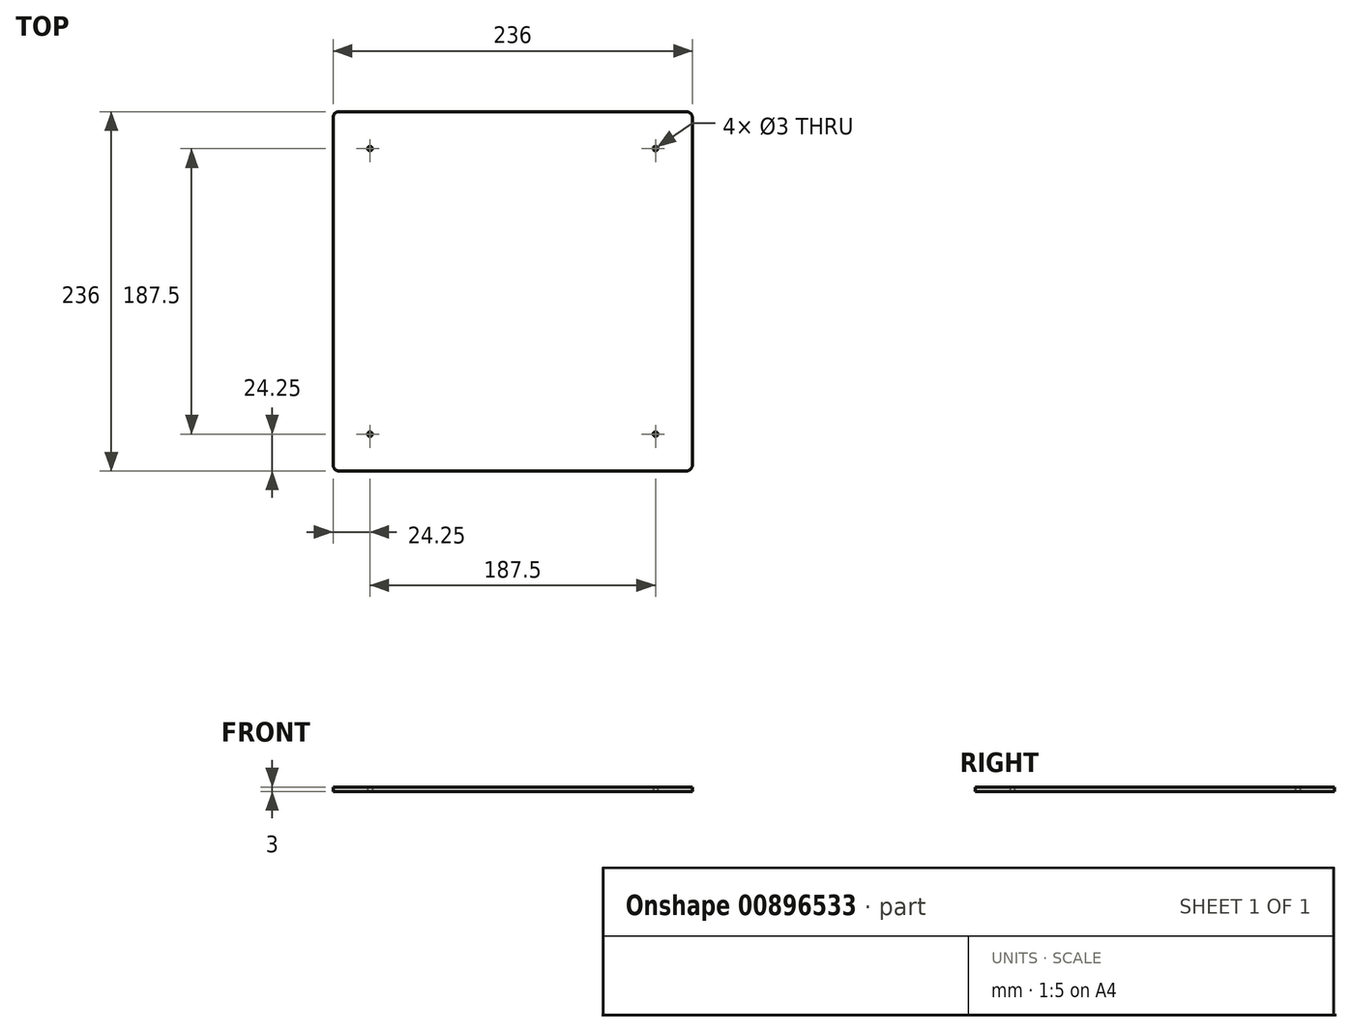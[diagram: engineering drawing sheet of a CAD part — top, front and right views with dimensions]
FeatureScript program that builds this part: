
annotation { "Feature Type Name" : "Feature", "Feature Type Description" : "" }
export const myFeature = defineFeature(function(context is Context, id is Id, definition is map)
    precondition{}
    {
        {
            assignVariable(context, id + "F0", {"variableType" : VariableType.LENGTH, "name" : "thickness", "lengthValue" : 3 * mm});
        }
        {
            var Q0;
            Q0=qCreatedBy(makeId("Top.planeOp"),FACE);
            var sketch = newSketch(context, id + "F1", { "sketchPlane" : qUnion([Q0])});
            skLineSegment(sketch, "E0.bottom", {"start": v(0, 0) * mm, "end": v(236, 0) * mm});
            skLineSegment(sketch, "E0.top", {"start": v(0, 236) * mm, "end": v(236, 236) * mm});
            skLineSegment(sketch, "E0.left", {"start": v(0, 0) * mm, "end": v(0, 236) * mm});
            skLineSegment(sketch, "E0.right", {"start": v(236, 0) * mm, "end": v(236, 236) * mm});
            skLineSegment(sketch, "E1.bottom", {"start": v(24.25, 24.25) * mm, "end": v(211.75, 24.25) * mm, "construction": true});
            skLineSegment(sketch, "E1.top", {"start": v(24.25, 211.75) * mm, "end": v(211.75, 211.75) * mm, "construction": true});
            skLineSegment(sketch, "E1.left", {"start": v(24.25, 24.25) * mm, "end": v(24.25, 211.75) * mm, "construction": true});
            skLineSegment(sketch, "E1.right", {"start": v(211.75, 24.25) * mm, "end": v(211.75, 211.75) * mm, "construction": true});
            skLineSegment(sketch, "E2", {"start": v(118, 236) * mm, "end": v(118, 211.75) * mm, "construction": true});
            skLineSegment(sketch, "E3", {"start": v(211.75, 118) * mm, "end": v(236, 118) * mm, "construction": true});
            skCircle(sketch, "E4", {"center": v(24.25, 211.75) * mm, "radius": 1.5 * mm});
            skCircle(sketch, "E5", {"center": v(211.75, 211.75) * mm, "radius": 1.5 * mm});
            skCircle(sketch, "E6", {"center": v(211.75, 24.25) * mm, "radius": 1.5 * mm});
            skCircle(sketch, "E7", {"center": v(24.25, 24.25) * mm, "radius": 1.5 * mm});
            skSolve(sketch);
        }
        {
            var Q0;
            Q0=qSketchRegion(id+"F1",true);
            extrude(context, id + "F2", {"entities" : qUnion([Q0]), "depth" : getVariable(context, 'thickness'), "offsetDistance" : 25 * mm});
        }
        {
            var Q0;
            Q0=makeQuery(id+"F2.opExtrude","SWEPT_EDGE",EDGE,{"disambiguationData":[OSD([sQuery(id+"F1.wireOp",EDGE,"E0.bottom"),sQuery(id+"F1.wireOp",EDGE,"E0.left")])]});
            var Q1;
            Q1=makeQuery(id+"F2.opExtrude","SWEPT_EDGE",EDGE,{"disambiguationData":[OSD([sQuery(id+"F1.wireOp",EDGE,"E0.top"),sQuery(id+"F1.wireOp",EDGE,"E0.left")])]});
            var Q2;
            Q2=makeQuery(id+"F2.opExtrude","SWEPT_EDGE",EDGE,{"disambiguationData":[OSD([sQuery(id+"F1.wireOp",EDGE,"E0.top"),sQuery(id+"F1.wireOp",EDGE,"E0.right")])]});
            var Q3;
            Q3=makeQuery(id+"F2.opExtrude","SWEPT_EDGE",EDGE,{"disambiguationData":[OSD([sQuery(id+"F1.wireOp",EDGE,"E0.bottom"),sQuery(id+"F1.wireOp",EDGE,"E0.right")])]});
            fillet(context, id + "F3", {"entities" : qUnion([Q0, Q1, Q2, Q3]), "radius" : 4 * mm, "tangentPropagation" : true, "allowEdgeOverflow" : false});
        }
    });
